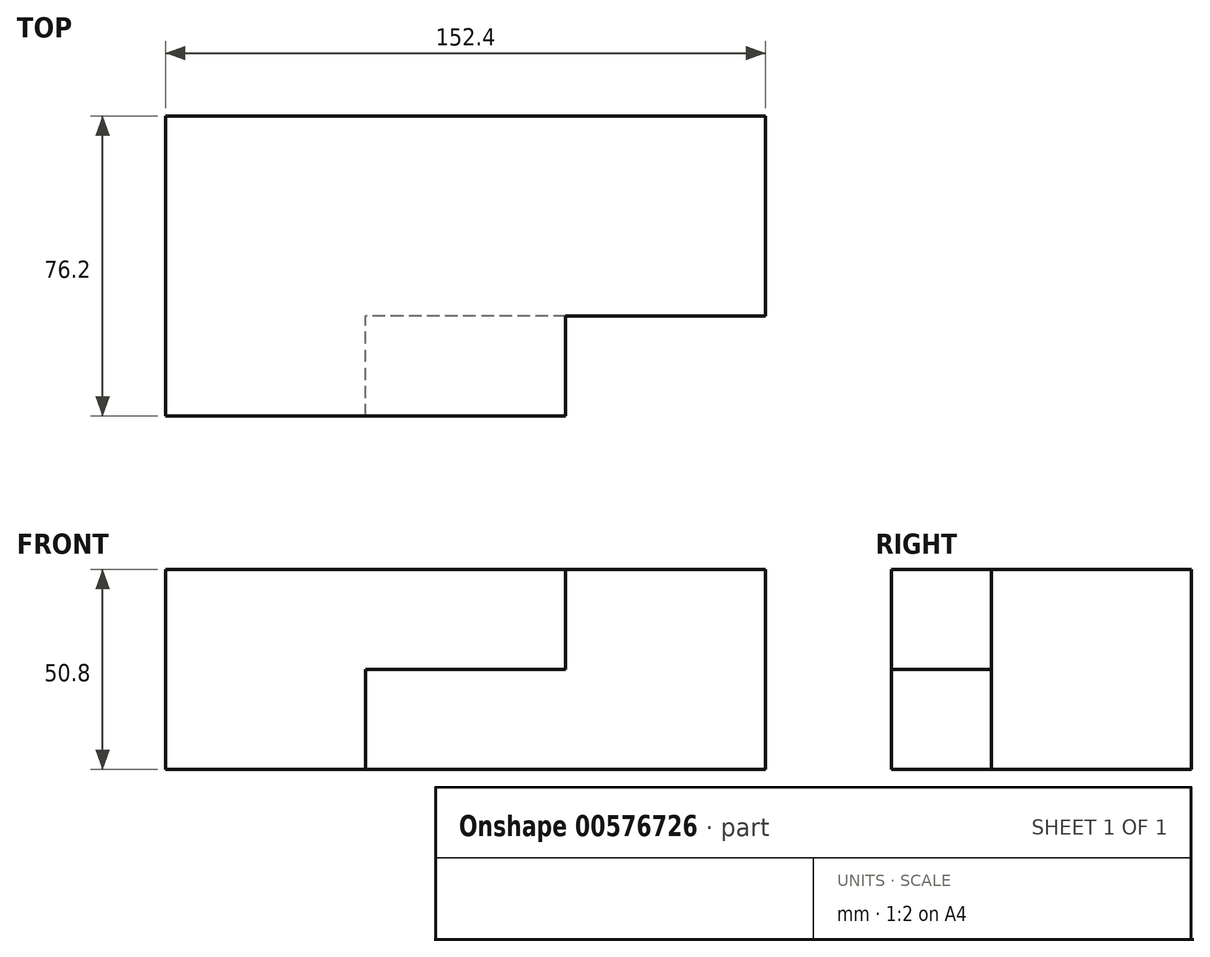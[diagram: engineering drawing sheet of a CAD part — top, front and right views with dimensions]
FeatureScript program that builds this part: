
annotation { "Feature Type Name" : "Feature", "Feature Type Description" : "" }
export const myFeature = defineFeature(function(context is Context, id is Id, definition is map)
    precondition{}
    {
        {
            var Q0;
            Q0=qCreatedBy(makeId("Front.planeOp"),FACE);
            var sketch = newSketch(context, id + "F0", { "sketchPlane" : qUnion([Q0])});
            skLineSegment(sketch, "E0", {"start": v(-78.05, 24.55) * mm, "end": v(74.35, 24.55) * mm});
            skLineSegment(sketch, "E1", {"start": v(74.35, 24.55) * mm, "end": v(74.35, -26.25) * mm});
            skLineSegment(sketch, "E2", {"start": v(74.35, -26.25) * mm, "end": v(-78.05, -26.25) * mm});
            skLineSegment(sketch, "E3", {"start": v(-78.05, -26.25) * mm, "end": v(-78.05, 24.55) * mm});
            skLineSegment(sketch, "E4", {"start": v(23.55, 24.55) * mm, "end": v(23.55, -0.85) * mm});
            skLineSegment(sketch, "E5", {"start": v(23.55, -0.85) * mm, "end": v(-27.25, -0.85) * mm});
            skLineSegment(sketch, "E6", {"start": v(-27.25, -0.85) * mm, "end": v(-27.25, -26.25) * mm});
            skSolve(sketch);
        }
        {
            var Q0;
            {var subQ1=sQuery(id+"F0.wireOp",EDGE,"E1");Q0=makeQuery(id+"F0.imprint","IMPRINT",FACE,{"disambiguationData":[TD([[makeQuery(id+"F0.imprint","IMPRINT",EDGE,{"derivedFrom":subQ1}),-1.0]])]});}
            extrude(context, id + "F1", {"entities" : qUnion([Q0]), "depth" : 50.8 * mm, "offsetDistance" : 25.4 * mm});
        }
        {
            var Q0;
            {var subQ1=sQuery(id+"F0.wireOp",EDGE,"E3");Q0=makeQuery(id+"F0.imprint","IMPRINT",FACE,{"disambiguationData":[TD([[makeQuery(id+"F0.imprint","IMPRINT",EDGE,{"derivedFrom":subQ1}),-1.0]])]});}
            extrude(context, id + "F2", {"entities" : qUnion([Q0]), "operationType" : NewBodyOperationType.ADD, "depth" : 76.2 * mm, "offsetDistance" : 25.4 * mm});
        }
    });
